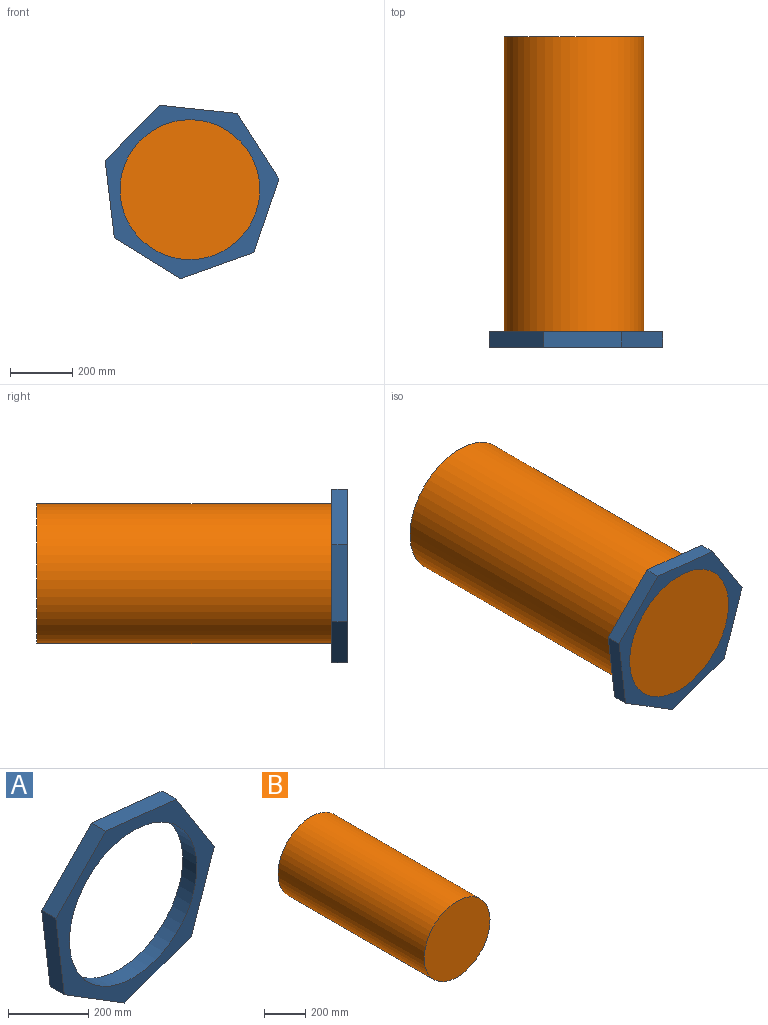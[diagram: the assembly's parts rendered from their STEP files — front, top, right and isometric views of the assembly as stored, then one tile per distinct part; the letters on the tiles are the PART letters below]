
ASSEMBLY  parts=2 mates=1
PART A: 10 faces, bbox 559.4x50x558.6 mm
  f0: plane 248.6x50mm, normal (-0.99,0,-0.12), area 12518.3mm2, adj f1,f7,f8,f9
  f1: plane 212.87x131.8mm, normal (-0.53,0,-0.85), area 12518.3mm2, adj f0,f2,f8,f9
  f2: plane 235.76x84.25mm, normal (0.34,0,-0.94), area 12518.3mm2, adj f1,f3,f8,f9
  f3: plane 236.86x81.13mm, normal (0.95,0,-0.32), area 12518.3mm2, adj f2,f4,f8,f9
  f4: plane 211.11x134.6mm, normal (0.84,0,0.54), area 12518.3mm2, adj f3,f5,f8,f9
  f5: plane 248.97x50mm, normal (0.11,0,0.99), area 12518.3mm2, adj f4,f7,f8,f9
  f6: cylinder r=225mm len=450mm, axis (0,1,0), area 70685.8mm2, adj f8,f9
  f7: plane 178.2x175.86mm, normal (-0.71,0,0.7), area 12518.3mm2, adj f0,f5,f8,f9
  f8: plane 559.43x558.6mm, normal (0,-1,0), area 68740.5mm2, adj f0,f1,f2,f3,f4,f5,f6,f7
  f9: plane 559.43x558.6mm, normal (0,1,0), area 68740.5mm2, adj f0,f1,f2,f3,f4,f5,f6,f7
PART B: 3 faces, bbox 450x1000x450 mm
  f0: cylinder r=225mm len=1000mm, axis (0,1,0), area 1413716.7mm2, adj f1,f2
  f1: plane 450x450mm, normal (0,-1,0), area 159043.1mm2, adj f0
  f2: plane 450x450mm, normal (0,1,0), area 159043.1mm2, adj f0
PLACE A t=(-59.11,-121.35,-152.29)mm
PLACE B t=(-59.11,828.65,-152.29)mm
MATE slider B.f0 <-> A.f6  axis (0,-1,0) through (-59.11,-171.35,-152.29)mm
